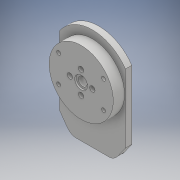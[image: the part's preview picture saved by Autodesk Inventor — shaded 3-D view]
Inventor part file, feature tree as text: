
AUTODESK INVENTOR PART (.ipt)
format: ipt  version: 2018 (Build 220112000, 112)  size: 201,728 bytes
history: native  units: mm
features: sketch x8, extrude x6, other x5, hole x2, pattern_circular x2, projected_geometry x2, reference x2
ambient origin geometry x8: Origin, YZ Plane, XZ Plane, XY Plane, X Axis, Y Axis, Z Axis, Center Point
bodies: Solid1 (feature_tree)
feature tree (27):
  extrude  "Extrusion1"  Depth=7.0mm TaperAngle=0.0deg
  extrude  "Extrusion2"  Depth=4.0mm TaperAngle=0.0deg
  hole  "Hole1"  [1 undecoded]
  pattern_circular  "Circular Pattern1"  [2 undecoded]
  extrude  "Extrusion3"  Depth=4.0mm TaperAngle=0.0deg
  extrude  "Extrusion4"  Depth=10.0mm TaperAngle=360.0deg
  extrude  "Extrusion5"  Depth=10.0mm
  pattern_circular  "Circular Pattern2"  [2 undecoded]
  hole  "Hole2"  [1 undecoded]
  extrude  "Extrusion6"  Depth=7.0mm
  sketch  "Sketch1"  dims[d0=40.0mm d1=7.0mm d2=0.0mm]
  sketch  "Sketch2"  dims[d3=80.4mm d4=4.0mm d5=0.0mm]
  sketch  "Sketch3"  dims[d6=7.0mm]
  sketch  "Sketch4"  dims[d7=3.3mm d8=6.35mm d9=6.3mm d10=2.0mm d11=90.0deg d12=8.0mm d13=20.594885mm d14=40.0mm d15=360.0deg]
  sketch  "Sketch5"  dims[d17=5.5mm]
  sketch  "Sketch6"  dims[d18=10.0mm d19=0.0mm]
  projected_geometry  "Projected Loop1"
  sketch  "Sketch8"  dims[d20=8.0mm]
  projected_geometry  "Projected Loop3"
  sketch  "Sketch9"  dims[d21=1.0mm d22=0.0mm d23=5.7mm d24=4.0mm d25=0.0mm d26=40.0mm d27=360.0deg d29=17.0mm d30=28.0mm d31=7.0mm d32=7.0mm d33=2.0mm d34=2.459mm d35=6.0mm d36=9.4mm d37=2.0mm d38=90.0deg d39=8.8mm d40=20.594885mm d41=10.0mm d42=0.0mm]
  reference  "Reference1"
  reference  "Reference2"
  parser-record x1  (decoder bookkeeping rows leaked as tree rows — omitted from the tree; the rows remain in map.json)
  other  "servocheck.iam"
  other  "bottomarm:1"
  other  "arm1half:1"
  other  "arm1:1"
note: 6 required parameter values undecoded (feature->parameter linkage not recoverable at this tier; creation-order binding heuristic only, values carry confidence <= 0.55)
note: 1 file-system path scrubbed to <path> (originals preserved in map.json)
